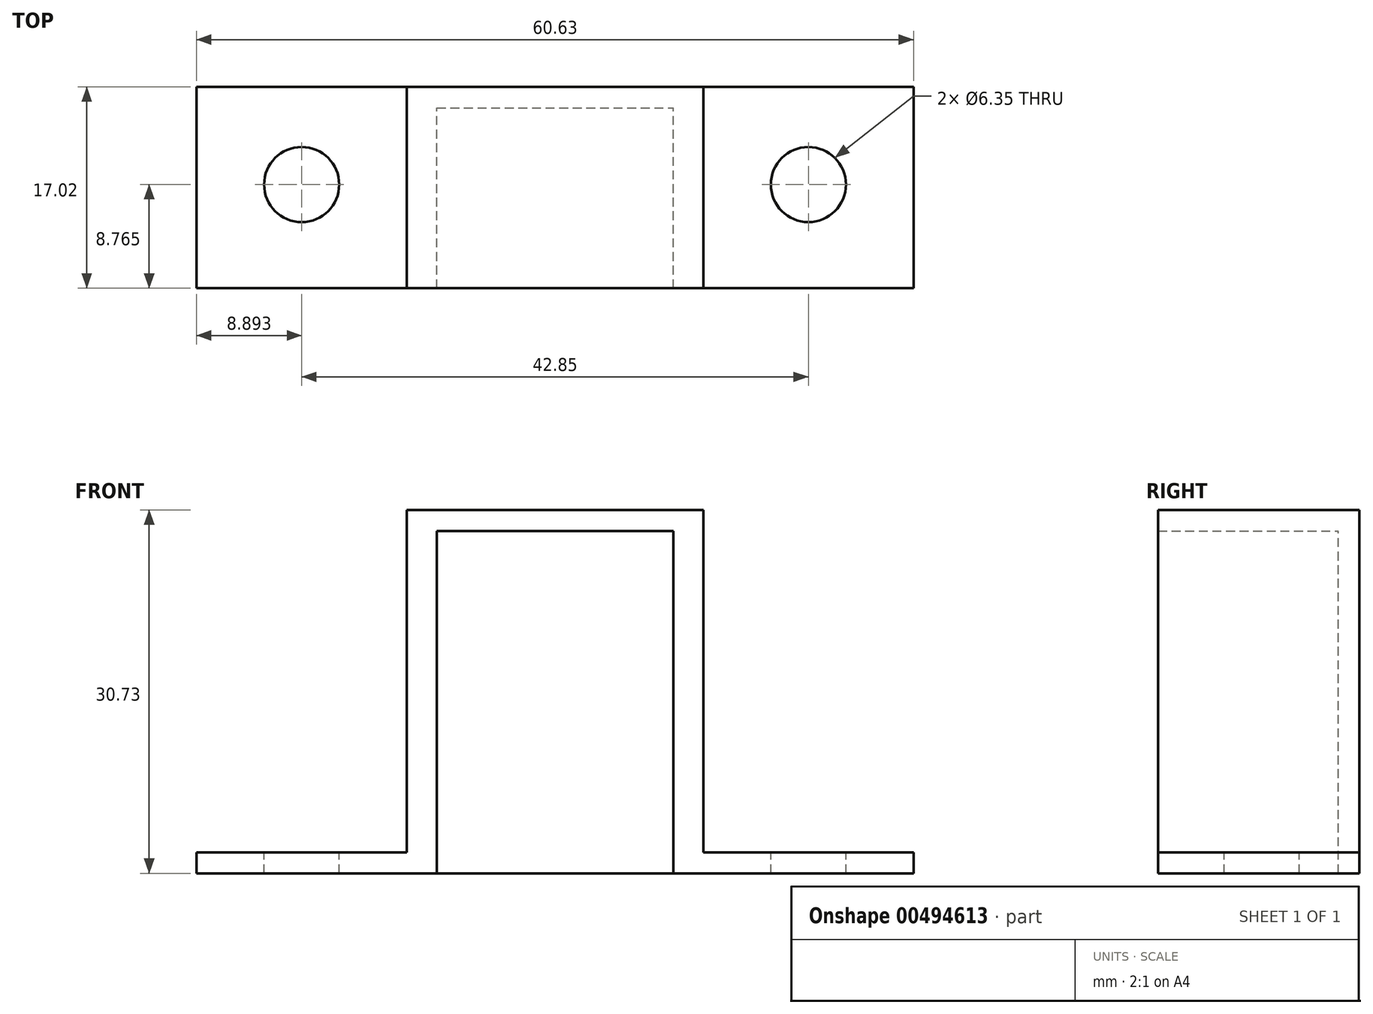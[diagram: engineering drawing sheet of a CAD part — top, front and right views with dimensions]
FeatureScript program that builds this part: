
annotation { "Feature Type Name" : "Feature", "Feature Type Description" : "" }
export const myFeature = defineFeature(function(context is Context, id is Id, definition is map)
    precondition{}
    {
        {
            var Q0;
            Q0=qCreatedBy(makeId("Front.planeOp"),FACE);
            var sketch = newSketch(context, id + "F0", { "sketchPlane" : qUnion([Q0])});
            skLineSegment(sketch, "E0", {"start": v(-30.08, -12.3) * mm, "end": v(-9.76, -12.3) * mm});
            skLineSegment(sketch, "E1", {"start": v(-9.76, -12.3) * mm, "end": v(-9.76, 16.66) * mm});
            skLineSegment(sketch, "E2", {"start": v(-9.76, 16.66) * mm, "end": v(10.23, 16.66) * mm});
            skLineSegment(sketch, "E3", {"start": v(10.23, 16.66) * mm, "end": v(10.23, -12.3) * mm});
            skLineSegment(sketch, "E4", {"start": v(10.23, -12.3) * mm, "end": v(30.55, -12.3) * mm});
            skLineSegment(sketch, "E5", {"start": v(-30.08, -10.52) * mm, "end": v(-12.3, -10.52) * mm});
            skLineSegment(sketch, "E6", {"start": v(-12.3, -10.52) * mm, "end": v(-12.3, 18.43) * mm});
            skLineSegment(sketch, "E7", {"start": v(-12.3, 18.43) * mm, "end": v(12.77, 18.43) * mm});
            skLineSegment(sketch, "E8", {"start": v(12.77, 18.43) * mm, "end": v(12.77, -10.52) * mm});
            skLineSegment(sketch, "E9", {"start": v(12.77, -10.52) * mm, "end": v(30.55, -10.52) * mm});
            skLineSegment(sketch, "E10", {"start": v(-30.08, -10.52) * mm, "end": v(-30.08, -12.3) * mm});
            skLineSegment(sketch, "E11", {"start": v(30.55, -10.52) * mm, "end": v(30.55, -12.3) * mm});
            skLineSegment(sketch, "E12.top", {"start": v(-12.3, -12.3) * mm, "end": v(12.77, -12.3) * mm});
            skLineSegment(sketch, "E12.left", {"start": v(-12.3, 18.43) * mm, "end": v(-12.3, -12.3) * mm});
            skLineSegment(sketch, "E12.right", {"start": v(12.77, 18.43) * mm, "end": v(12.77, -12.3) * mm});
            skSolve(sketch);
        }
        {
            var Q0;
            {var subQ6=sQuery(id+"F0.wireOp",EDGE,"E1");Q0=makeQuery(id+"F0.imprint","IMPRINT",FACE,{"disambiguationData":[TD([[makeQuery(id+"F0.imprint","IMPRINT",EDGE,{"derivedFrom":subQ6}),1.0]])]});}
            var Q1;
            {var subQ0=sQuery(id+"F0.wireOp",EDGE,"E0");Q1=makeQuery(id+"F0.imprint","IMPRINT",FACE,{"disambiguationData":[TD([[makeQuery(id+"F0.imprint","IMPRINT",EDGE,{"derivedFrom":subQ0}),1.0]])]});}
            var Q2;
            {var subQ0=sQuery(id+"F0.wireOp",EDGE,"E4");Q2=makeQuery(id+"F0.imprint","IMPRINT",FACE,{"disambiguationData":[TD([[makeQuery(id+"F0.imprint","IMPRINT",EDGE,{"derivedFrom":subQ0}),1.0]])]});}
            extrude(context, id + "F1", {"entities" : qUnion([Q0, Q1, Q2]), "depth" : 17.02 * mm, "offsetDistance" : 25.4 * mm});
        }
        {
            var Q0;
            {var subQ0=sQuery(id+"F0.wireOp",EDGE,"E1");Q0=makeQuery(id+"F0.imprint","IMPRINT",FACE,{"disambiguationData":[TD([[makeQuery(id+"F0.imprint","IMPRINT",EDGE,{"derivedFrom":subQ0}),-1.0]])]});}
            extrude(context, id + "F2", {"entities" : qUnion([Q0]), "operationType" : NewBodyOperationType.ADD, "depth" : 1.78 * mm});
        }
        {
            var Q0;
            Q0=makeQuery(id+"F1.opExtrude","SWEPT_FACE",FACE,{"disambiguationData":[OSD([sQuery(id+"F0.wireOp",EDGE,"E7")])]});
            var sketch = newSketch(context, id + "F3", { "sketchPlane" : qUnion([Q0])});
            skCircle(sketch, "E13", {"center": v(0, -8.25) * mm, "radius": 3.81 * mm});
            skSolve(sketch);
        }
        {
            var Q0;
            Q0=makeQuery(id+"F1.opExtrude","SWEPT_FACE",FACE,{"disambiguationData":[OSD([sQuery(id+"F0.wireOp",EDGE,"E5")])]});
            var sketch = newSketch(context, id + "F4", { "sketchPlane" : qUnion([Q0])});
            skCircle(sketch, "E14", {"center": v(-21.19, -8.26) * mm, "radius": 3.18 * mm});
            skSolve(sketch);
        }
        {
            var Q0;
            Q0=makeQuery(id+"F1.opExtrude","SWEPT_FACE",FACE,{"disambiguationData":[OSD([sQuery(id+"F0.wireOp",EDGE,"E9")])]});
            var sketch = newSketch(context, id + "F5", { "sketchPlane" : qUnion([Q0])});
            skCircle(sketch, "E15", {"center": v(21.66, -8.26) * mm, "radius": 3.18 * mm});
            skSolve(sketch);
        }
        {
            var Q0;
            Q0 = qSketchRegion(id + "F5", true);
            var Q1;
            Q1 = qSketchRegion(id + "F4", true);
            var Q2;
            Q2 = qSketchRegion(id + "F3", true);
            extrude(context, id + "F6", {"entities" : qUnion([Q0, Q1, Q2]), "operationType" : NewBodyOperationType.REMOVE, "oppositeDirection" : true, "depth" : 25.4 * mm});
        }
    });
